# Revit family: S-31 (EN)
name_source: partatom
category: Pipe Fittings
revit_build: Autodesk Revit 2015 (Build: 20140606_1530(x64)
units: mm (PartAtom-declared; Revit-internal decimal feet)

## types (3) — shared parameters
Appliances = WASH BASIN, BIDET
Caudal = 0.4 L/s
Description = SINK TRAP, ADJUSTABLE S TRAP, HORIZONTAL OUTLET, WITH LOOSE NUT
Manufacturer = Jimten
Material = PP (White)
Model = S-31
URL = http://www.jimten.com

## per-type parameters (varying)
| type | Amax | Amin | Inlets | Outlet | Reference | S | r |
| S-31_1 1/2" | 230 mm  [stored 0.754593 ft] | 170 mm  [stored 0.557743 ft] | 1 1/2'' FEMALE THREAD | Ø40 MM (FEMALE) | 006028 | 40 mm  [stored 0.131234 ft] | 38 mm |
| S-31_1 1/4" x 1 1/2" | 230 mm  [stored 0.754593 ft] | 170 mm  [stored 0.557743 ft] | 1 1/4'' FEMALE THREAD | Ø40 MM (FEMALE) | 006366 | 40 mm  [stored 0.131234 ft] | 32 mm  [stored 0.104987 ft] |
| S-31_1 1/4" | 210 mm  [stored 0.688976 ft] | 163 mm  [stored 0.534777 ft] | 1 1/4'' FEMALE THREAD | Ø32 MM (FEMALE) | 006046 | 32 mm  [stored 0.104987 ft] | 32 mm  [stored 0.104987 ft] |

note: [stored X ft] marks values corroborated as IEEE doubles in the binary element streams (Revit-internal decimal feet)

## geometry (parser evidence)
native form markers: Blend x2
no freeform markers — native parametric forms only
